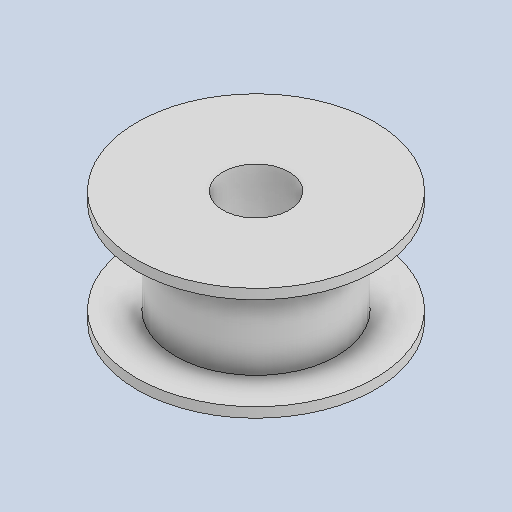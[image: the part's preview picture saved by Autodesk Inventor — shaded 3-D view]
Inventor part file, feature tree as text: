
AUTODESK INVENTOR PART (.ipt)
format: ipt  version: 2024.2 (Build 282272000, 272)  size: 111,104 bytes
history: native  units: in
note: dims shown in document units (in); Inventor stores cm internally (conversion verified against a paired STEP export)
features: revolve x1
ambient origin geometry x8: Origin, YZ Plane, XZ Plane, XY Plane, X Axis, Y Axis, Z Axis, Center Point
bodies: Solid1 (feature_tree)
feature tree (1):
  revolve  "Revolve1"  [1 undecoded]
note: 1 required parameter value undecoded (feature->parameter linkage not recoverable at this tier; creation-order binding heuristic only, values carry confidence <= 0.55)
